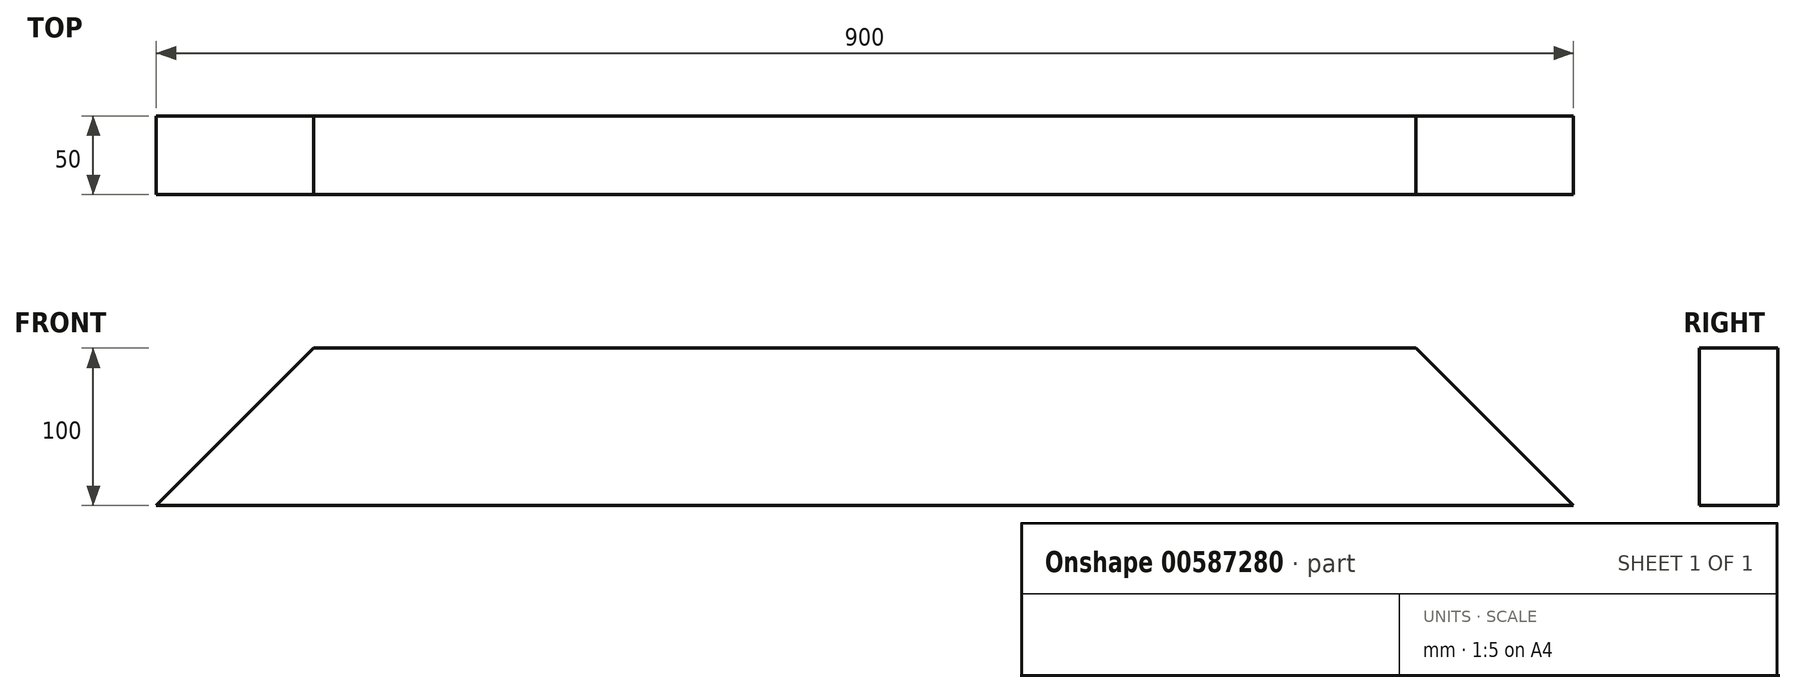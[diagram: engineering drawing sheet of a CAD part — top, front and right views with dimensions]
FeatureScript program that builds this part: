
annotation { "Feature Type Name" : "Feature", "Feature Type Description" : "" }
export const myFeature = defineFeature(function(context is Context, id is Id, definition is map)
    precondition{}
    {
        {
            var Q0;
            Q0=qCreatedBy(makeId("Front.planeOp"),FACE);
            var sketch = newSketch(context, id + "F0", { "sketchPlane" : qUnion([Q0])});
            skLineSegment(sketch, "E0", {"start": v(-1250, 0) * mm, "end": v(1250, 0) * mm, "construction": true});
            skLineSegment(sketch, "E1", {"start": v(1250, 0) * mm, "end": v(0, 1250) * mm, "construction": true});
            skLineSegment(sketch, "E2", {"start": v(0, 1250) * mm, "end": v(-1250, 0) * mm, "construction": true});
            skLineSegment(sketch, "E3", {"start": v(0, 1250) * mm, "end": v(0, 1250) * mm});
            skLineSegment(sketch, "E4", {"start": v(-1250, 0) * mm, "end": v(-1250, 0) * mm});
            skLineSegment(sketch, "E5", {"start": v(-1250, 0) * mm, "end": v(0, 1250) * mm, "construction": true});
            skLineSegment(sketch, "E6", {"start": v(-350, 900) * mm, "end": v(350, 900) * mm});
            skLineSegment(sketch, "E7", {"start": v(-350, 900) * mm, "end": v(-450, 800) * mm});
            skLineSegment(sketch, "E8", {"start": v(-450, 800) * mm, "end": v(450, 800) * mm});
            skLineSegment(sketch, "E9", {"start": v(450, 800) * mm, "end": v(350, 900) * mm});
            skPoint(sketch, "E10", {"position": v(0, 800) * mm});
            skPoint(sketch, "E11", {"position": v(0, 900) * mm});
            skSolve(sketch);
        }
        {
            var Q0;
            Q0=makeQuery(id+"F0.imprint","IMPRINT",FACE,{"disambiguationData":[TD([[makeQuery(id+"F0.imprint","IMPRINT",EDGE,{"derivedFrom":sQuery(id+"F0.wireOp",EDGE,"E6")}),-1.0]])]});
            extrude(context, id + "F1", {"entities" : qUnion([Q0]), "depth" : 50 * mm, "offsetDistance" : 25 * mm});
        }
    });
